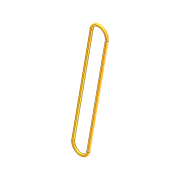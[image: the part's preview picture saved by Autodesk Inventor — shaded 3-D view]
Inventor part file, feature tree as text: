
AUTODESK INVENTOR PART (.ipt)
format: ipt  version: 2012 (Build 160160000, 160)  size: 92,672 bytes
history: native  units: in
note: dims shown in document units (in); Inventor stores cm internally (conversion verified against a paired STEP export)
features: extrude x1, fillet x1, sketch x1
ambient origin geometry x8: Origin, YZ Plane, XZ Plane, XY Plane, X Axis, Y Axis, Z Axis, Center Point
bodies: Solid1 (feature_tree)
feature tree (3):
  extrude  "Extrusion1"  Depth=0.1875in
  fillet  "Fillet1"  Radius=0.1875in
  sketch  "Sketch1"  dims[d0=0.625in d1=0.1875in d2=0.1875in d3=0.0in d4=0.0938in]
